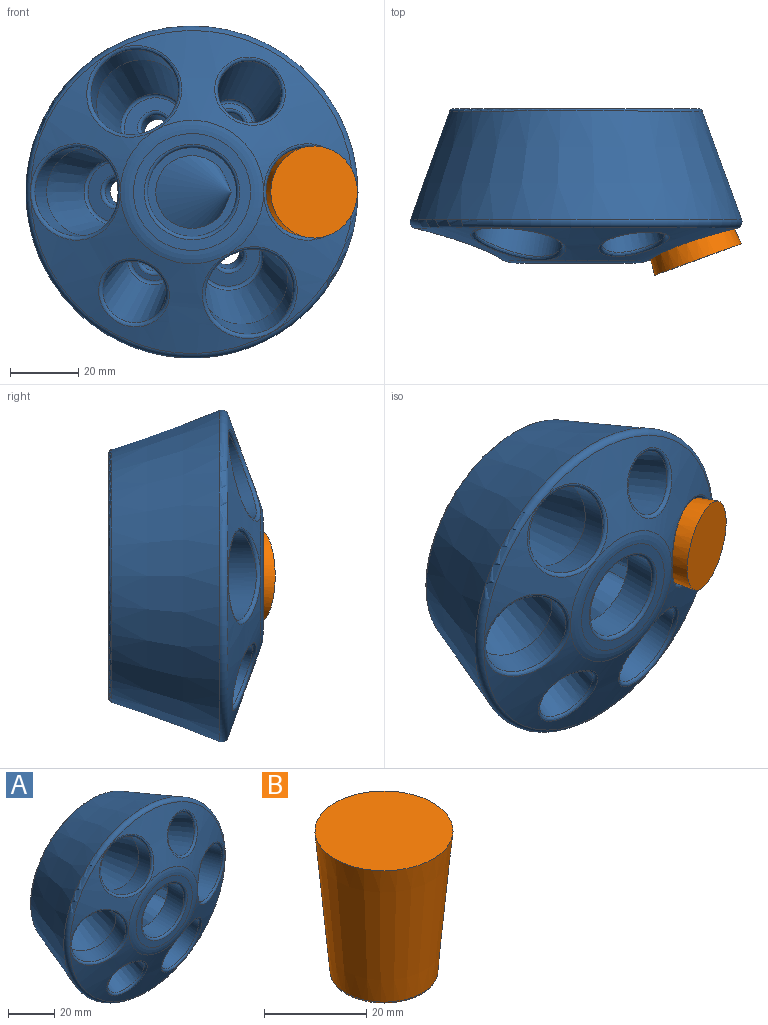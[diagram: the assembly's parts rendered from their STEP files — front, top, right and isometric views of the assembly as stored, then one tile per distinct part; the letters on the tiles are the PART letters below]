
ASSEMBLY  parts=2 mates=1
PART A: 57 faces, bbox 111.1x53.8x111.1 mm
  f0: torus R=5mm, axis (0.17,-0.94,0.3), area 43.1mm2, adj f1,f37
  f1: cylinder r=4mm len=9.51mm, axis (0.17,-0.94,0.3), area 158.4mm2, adj f0,f24
  f2: torus R=5mm, axis (-0.17,-0.94,0.3), area 43.1mm2, adj f3,f29
  f3: cylinder r=4mm len=9.78mm, axis (-0.17,-0.94,0.3), area 144.8mm2, adj f2,f24
  f4: torus R=5mm, axis (-0.34,-0.94,0), area 43.1mm2, adj f5,f31
  f5: cylinder r=4mm len=9.99mm, axis (-0.34,-0.94,0), area 144.8mm2, adj f4,f24
  f6: torus R=5mm, axis (-0.17,-0.94,-0.3), area 43.1mm2, adj f7,f36
  f7: cylinder r=4mm len=11.41mm, axis (-0.17,-0.94,-0.3), area 195mm2, adj f6,f24
  f8: torus R=5mm, axis (0.17,-0.94,-0.3), area 43.1mm2, adj f9,f33
  f9: cylinder r=4mm len=9.78mm, axis (0.17,-0.94,-0.3), area 144.8mm2, adj f8,f24
  f10: cone r=48.53mm half-angle=20deg, axis (0,-1,0), area 9063.9mm2, adj f21,f45
  f11: cone r=13mm half-angle=7.4deg, axis (0.34,-0.94,0), area 1715.4mm2, adj f34,f50
  f12: cone r=9.5mm half-angle=3.4deg, axis (0.17,-0.94,0.3), area 1682mm2, adj f43,f53
  f13: cone r=9.5mm half-angle=3.4deg, axis (-0.17,-0.94,-0.3), area 1689.1mm2, adj f40,f54
  f14: cone r=13mm half-angle=7.4deg, axis (-0.34,-0.94,0), area 1715.4mm2, adj f30,f56
  f15: cone r=13mm half-angle=7.4deg, axis (0.17,-0.94,-0.3), area 1715.4mm2, adj f32,f51
  f16: cone r=13mm half-angle=7.4deg, axis (-0.17,-0.94,0.3), area 1715.4mm2, adj f28,f55
  f17: cone r=21.02mm half-angle=70deg, axis (0,1,0), area 388.9mm2, adj f21,f22,f41,f42
  f18: cone r=21.02mm half-angle=70deg, axis (0,1,0), area 692.2mm2, adj f21,f22,f42,f43,f44
  f19: cone r=21.02mm half-angle=70deg, axis (0,1,0), area 451mm2, adj f21,f22,f39,f44
  f20: cone r=21.02mm half-angle=70deg, axis (0,1,0), area 1072.2mm2, adj f21,f22,f39,f40,f41
  f21: torus R=46.65mm, axis (0,-1,0), area 953.1mm2, adj f10,f17,f18,f19,f20
  f22: torus R=17.14mm, axis (0,-1,0), area 475.2mm2, adj f17,f18,f19,f20,f23
  f23: plane 34.29x34.29mm, normal (0,-1,0), area 307.6mm2, adj f22,f38
  f24: plane 77.93x77.93mm, normal (0,1,0), area 3712mm2, adj f1,f3,f5,f7,f9,f45,f46,f48
  f25: plane 17.84x17.84mm, normal (0,-1,0), area 171.5mm2, adj f47,f52
  f26: cone r=9.8mm half-angle=7.4deg, axis (0,-1,0), area 1715.4mm2, adj f27,f52
  f27: cylinder r=13mm len=26mm, axis (0,-1,0), area 816.8mm2, adj f26,f38
  f28: cylinder r=13mm len=27.75mm, axis (0.17,0.94,-0.3), area 770.5mm2, adj f16,f44
  f29: plane 17.58x17.04mm, normal (-0.17,-0.94,0.3), area 171.5mm2, adj f2,f55
  f30: cylinder r=13mm len=27.85mm, axis (0.34,0.94,0), area 798.8mm2, adj f14,f39
  f31: plane 17.84x16.77mm, normal (-0.34,-0.94,0), area 171.5mm2, adj f4,f56
  f32: cylinder r=13mm len=27.69mm, axis (-0.17,0.94,0.3), area 766.5mm2, adj f15,f41
  f33: plane 17.58x17.04mm, normal (0.17,-0.94,-0.3), area 171.5mm2, adj f8,f51
  f34: cylinder r=13mm len=27.85mm, axis (-0.34,0.94,0), area 792.7mm2, adj f11,f42
  f35: plane 17.84x16.77mm, normal (0.34,-0.94,0), area 171.5mm2, adj f49,f50
  f36: plane 12.92x12.53mm, normal (-0.17,-0.94,-0.3), area 56.6mm2, adj f6,f54
  f37: plane 12.92x12.53mm, normal (0.17,-0.94,0.3), area 56.6mm2, adj f0,f53
  f38: torus R=14mm, axis (0,-1,0), area 131.9mm2, adj f23,f27
  f39: bspline ~28.25x26.3mm, area 138.6mm2, adj f19,f20,f30
  f40: bspline ~20.68x19.99mm, area 96.8mm2, adj f13,f20
  f41: bspline ~27.83x26.9mm, area 138.1mm2, adj f17,f20,f32
  f42: bspline ~28.24x26.29mm, area 138.4mm2, adj f17,f18,f34
  f43: bspline ~20.69x19.99mm, area 193.2mm2, adj f12,f18
  f44: bspline ~27.84x26.89mm, area 137.9mm2, adj f18,f19,f28
  f45: torus R=36.05mm, axis (0,1,0), area 280.9mm2, adj f10,f24
  f46: cylinder r=4mm len=8.68mm, axis (0,-1,0), area 218.2mm2, adj f24,f47
  f47: torus R=5mm, axis (0,-1,0), area 43.1mm2, adj f25,f46
  f48: cylinder r=4mm len=9.99mm, axis (0.34,-0.94,0), area 144.8mm2, adj f24,f49
  f49: torus R=5mm, axis (0.34,-0.94,0), area 43.1mm2, adj f35,f48
  f50: torus R=8.92mm, axis (0.34,-0.94,0), area 86.2mm2, adj f11,f35
  f51: torus R=8.92mm, axis (0.17,-0.94,-0.3), area 86.2mm2, adj f15,f33
  f52: torus R=8.92mm, axis (0,-1,0), area 86.2mm2, adj f25,f26
  f53: torus R=6.56mm, axis (0.17,-0.94,0.3), area 68.2mm2, adj f12,f37
  f54: torus R=6.56mm, axis (-0.17,-0.94,-0.3), area 68.2mm2, adj f13,f36
  f55: torus R=8.92mm, axis (-0.17,-0.94,0.3), area 86.2mm2, adj f16,f29
  f56: torus R=8.92mm, axis (-0.34,-0.94,0), area 86.2mm2, adj f14,f31
PART B: 4 faces, bbox 27x27x34 mm
  f0: plane 20.08x20.08mm, normal (0,0,-1), area 316.8mm2, adj f3
  f1: plane 27x27mm, normal (0,0,1), area 572.6mm2, adj f2
  f2: cone r=13.5mm half-angle=5deg, axis (0,0,1), area 2543.2mm2, adj f1,f3
  f3: torus R=10.04mm, axis (0,0,1), area 48.2mm2, adj f0,f2
PLACE A at identity
PLACE B rot(axis=(0.97,0.17,0.17),91.7deg) t=(24.16,-12.18,0)mm
MATE slider B.f2 <-> A.f48  axis (0.34,-0.94,0) through (30.05,-28.37,0)mm
